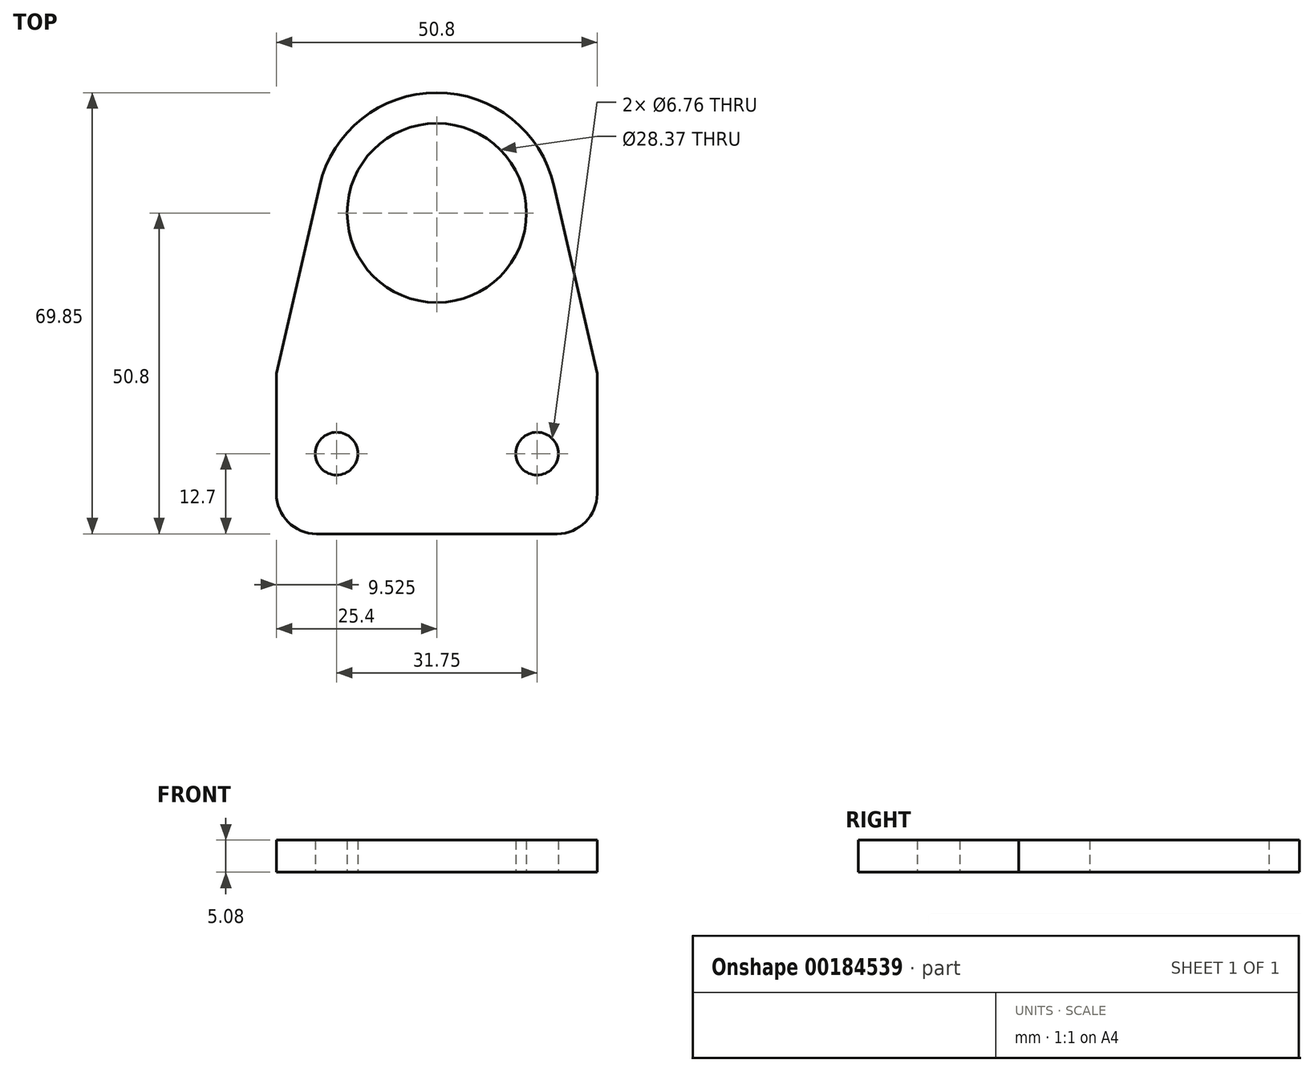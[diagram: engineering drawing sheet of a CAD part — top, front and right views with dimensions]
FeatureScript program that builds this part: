
annotation { "Feature Type Name" : "Feature", "Feature Type Description" : "" }
export const myFeature = defineFeature(function(context is Context, id is Id, definition is map)
    precondition{}
    {
        {
            var Q0;
            Q0=qCreatedBy(makeId("Top.planeOp"),FACE);
            var sketch = newSketch(context, id + "F0", { "sketchPlane" : qUnion([Q0])});
            skLineSegment(sketch, "E0.bottom", {"start": v(19.05, -12.7) * mm, "end": v(-19.05, -12.7) * mm});
            skLineSegment(sketch, "E0.left", {"start": v(25.4, -6.35) * mm, "end": v(25.4, 12.7) * mm});
            skLineSegment(sketch, "E0.right", {"start": v(-25.4, -6.35) * mm, "end": v(-25.4, 12.7) * mm});
            skPoint(sketch, "E0.middle", {"position": v(0, 0) * mm});
            skCircle(sketch, "E1", {"center": v(0, 38.1) * mm, "radius": 14.19 * mm});
            skArc(sketch, "E2", {"start": v(18.56, 42.38) * mm, "mid": v(0, 57.15) * mm, "end": v(-18.56, 42.38) * mm});
            skLineSegment(sketch, "E3", {"start": v(-25.4, 12.7) * mm, "end": v(-18.56, 42.38) * mm});
            skLineSegment(sketch, "E4", {"start": v(25.4, 12.7) * mm, "end": v(18.56, 42.38) * mm});
            skPoint(sketch, "E5.visualSharp", {"position": v(-25.4, -12.7) * mm});
            skArc(sketch, "E5.filletArc", {"start": v(-25.4, -6.35) * mm, "mid": v(-23.54, -10.84) * mm, "end": v(-19.05, -12.7) * mm});
            skPoint(sketch, "E6.visualSharp", {"position": v(25.4, -12.7) * mm});
            skArc(sketch, "E6.filletArc", {"start": v(19.05, -12.7) * mm, "mid": v(23.54, -10.84) * mm, "end": v(25.4, -6.35) * mm});
            skCircle(sketch, "E7", {"center": v(-15.88, 0) * mm, "radius": 3.38 * mm});
            skCircle(sketch, "E8.MirrorC", {"center": v(15.88, 0) * mm, "radius": 3.38 * mm});
            skSolve(sketch);
        }
        {
            var Q0;
            Q0=makeQuery(id+"F0.imprint","IMPRINT",FACE,{"disambiguationData":[TD([[makeQuery(id+"F0.imprint","IMPRINT",EDGE,{"derivedFrom":sQuery(id+"F0.wireOp",EDGE,"E0.bottom")}),-1.0]])]});
            extrude(context, id + "F1", {"entities" : qUnion([Q0]), "depth" : 5.08 * mm});
        }
    });
